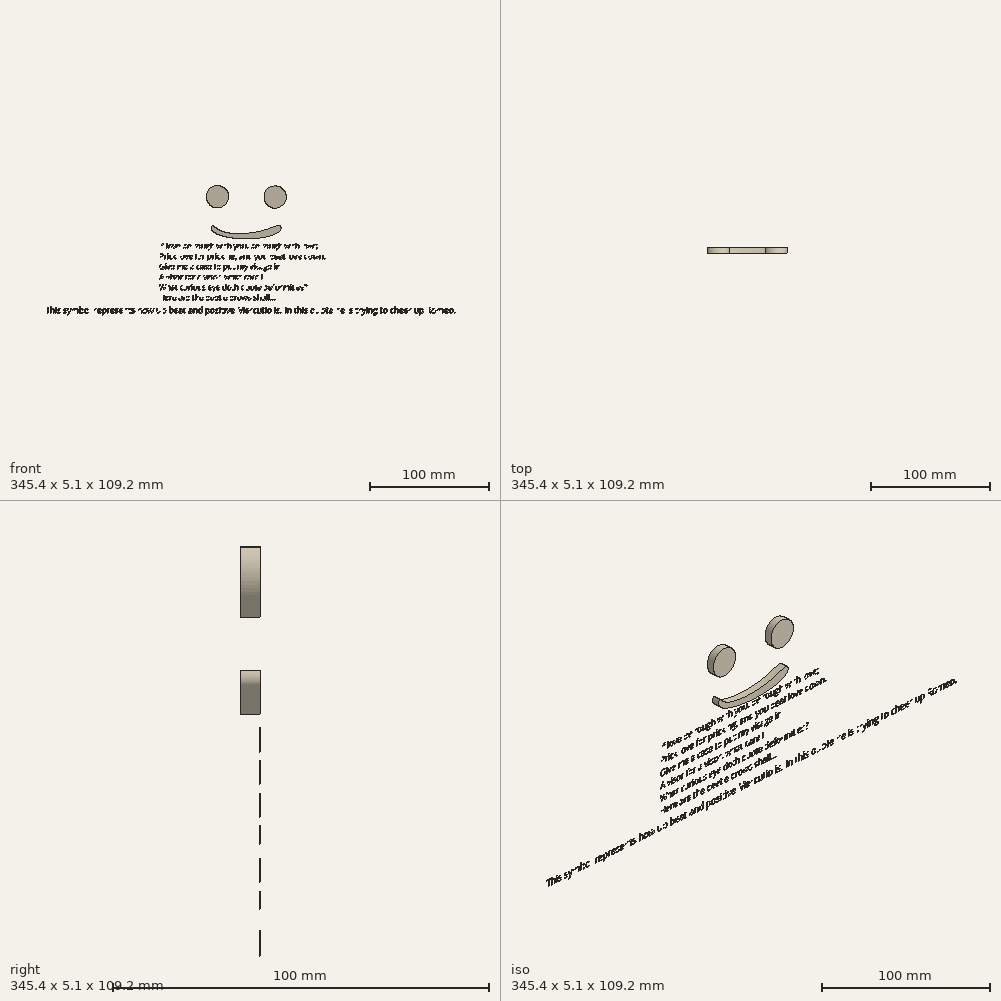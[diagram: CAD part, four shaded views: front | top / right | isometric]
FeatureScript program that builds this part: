
annotation { "Feature Type Name" : "Feature", "Feature Type Description" : "" }
export const myFeature = defineFeature(function(context is Context, id is Id, definition is map)
    precondition{}
    {
        {
            var Q0;
            Q0=qCreatedBy(makeId("Front.planeOp"),FACE);
            var sketch = newSketch(context, id + "F0", { "sketchPlane" : qUnion([Q0])});
            skCircle(sketch, "E0", {"center": v(-20.11, 11.19) * mm, "radius": 9.4 * mm});
            skCircle(sketch, "E1", {"center": v(28.51, 10.97) * mm, "radius": 9.4 * mm});
            skLineSegment(sketch, "E2", {"start": v(-20.11, 11.19) * mm, "end": v(4.2, 11.19) * mm});
            skLineSegment(sketch, "E3", {"start": v(4.2, 11.19) * mm, "end": v(28.51, 10.97) * mm});
            skEllipse(sketch, "E4", {"center": v(4.2, -15.45) * mm, "majorRadius": 29.34 * mm, "minorRadius": 8.83 * mm, "majorAxis": v(1, 0)});
            skPoint(sketch, "E5.5.internal.snap0", {"position": v(-25.14, -15.45) * mm});
            skFitSpline(sketch, "E6", {"points": [v(-23.81, -12.82) * mm, v(-18.37, -17) * mm, v(-7.11, -19.55) * mm, v(5.46, -19.4) * mm, v(15.93, -17.89) * mm, v(23.73, -15.45) * mm, v(31.87, -12.5) * mm, v(31.8, -12.46) * mm], "startDerivative": vector(34.1, -33.06) * mm, "endDerivative": vector(-6.9, 2.87) * mm});
            skSolve(sketch);
        }
        {
            var Q0;
            {var subQ0=sQuery(id+"F0.wireOp",EDGE,"E6");var subQ1=sQuery(id+"F0.wireOp",EDGE,"E4");var subQ2=makeQuery(id+"F0.imprint","INTERSECT",VERTEX,{"disambiguationData":[OD(0.0)],"derivedFrom":[subQ1,subQ0]});Q0=makeQuery(id+"F0.imprint","IMPRINT",FACE,{"disambiguationData":[TD([[makeQuery(id+"F0.imprint","IMPRINT",EDGE,{"disambiguationData":[TD([[subQ2,-1.0]])],"derivedFrom":subQ1}),1.0]])]});}
            var Q1;
            Q1=makeQuery(id+"F0.imprint","IMPRINT",FACE,{"disambiguationData":[TD([[makeQuery(id+"F0.imprint","IMPRINT",EDGE,{"derivedFrom":sQuery(id+"F0.wireOp",EDGE,"E0")}),1.0]])]});
            var Q2;
            Q2=makeQuery(id+"F0.imprint","IMPRINT",FACE,{"disambiguationData":[TD([[makeQuery(id+"F0.imprint","IMPRINT",EDGE,{"derivedFrom":sQuery(id+"F0.wireOp",EDGE,"E1")}),1.0]])]});
            extrude(context, id + "F1", {"entities" : qUnion([Q0, Q1, Q2]), "depth" : 5.08 * mm, "offsetDistance" : 25.4 * mm});
        }
        {
            var Q0;
            Q0=qCreatedBy(makeId("Front.planeOp"),FACE);
            var sketch = newSketch(context, id + "F2", { "sketchPlane" : qUnion([Q0])});
            skText(sketch, "E7", { "text": "If love be rough with you, be rough with love; \nPrick love for pricking, and you beat love down. \nGive me a case to put my visage in: \nA visor for a visor! what care I \nWhat curious eye doth quote deformities? \nHere are the beetle brows shall...", "fontName": "OpenSans-Regular.ttf"});
            const initialGuessF2  = {"E7": [-0.06913, -0.03263, 1, 0, 0.0046]};
            skSetInitialGuess(sketch, initialGuessF2);
            skSolve(sketch);
        }
        {
            var Q0;
            Q0=qCreatedBy(makeId("Front.planeOp"),FACE);
            var sketch = newSketch(context, id + "F3", { "sketchPlane" : qUnion([Q0])});
            skText(sketch, "E8", { "text": "This symbol represents how up beat and positive Mercutio is. In this quote he is trying to cheer up Romeo.", "fontName": "OpenSans-Regular.ttf"});
            const initialGuessF3  = {"E8": [-0.16513, -0.08693, 1, 0, 0.00504]};
            skSetInitialGuess(sketch, initialGuessF3);
            skSolve(sketch);
        }
        {
            var Q0;
            Q0 = qSketchRegion(id + "F2", true);
            var Q1;
            Q1 = qSketchRegion(id + "F3", true);
            extrude(context, id + "F4", {"entities" : qUnion([Q0, Q1]), "depth" : 0.05 * mm, "offsetDistance" : 25.4 * mm});
        }
    });
